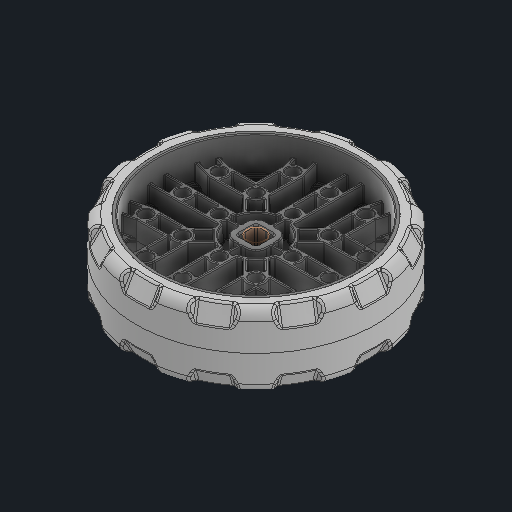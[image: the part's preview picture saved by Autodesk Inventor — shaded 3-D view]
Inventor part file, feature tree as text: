
AUTODESK INVENTOR PART (.ipt)
format: ipt  version: 2024 (Build 280153000, 153)  size: 12,597,760 bytes
history: native  units: in
note: dims shown in document units (in); Inventor stores cm internally (conversion verified against a paired STEP export)
features: other x6, sketch x1
ambient origin geometry x8: Origin, YZ Plane, XZ Plane, XY Plane, X Axis, Y Axis, Z Axis, Center Point
bodies: Solid1 (feature_tree), Solid2 (feature_tree)
feature tree (7):
  other  "3.25 Traction Antistatic.ipt"
  other  "Solid1::3.25 Traction Antistatic.ipt"
  other  "Solid2::3.25 Traction Antistatic.ipt"
  other  "TaggingFeature1"
  sketch  "Sketch1"  dims[d0=0.3937in]
  other  "Srf1"
  other  "Srf1::Derived"
